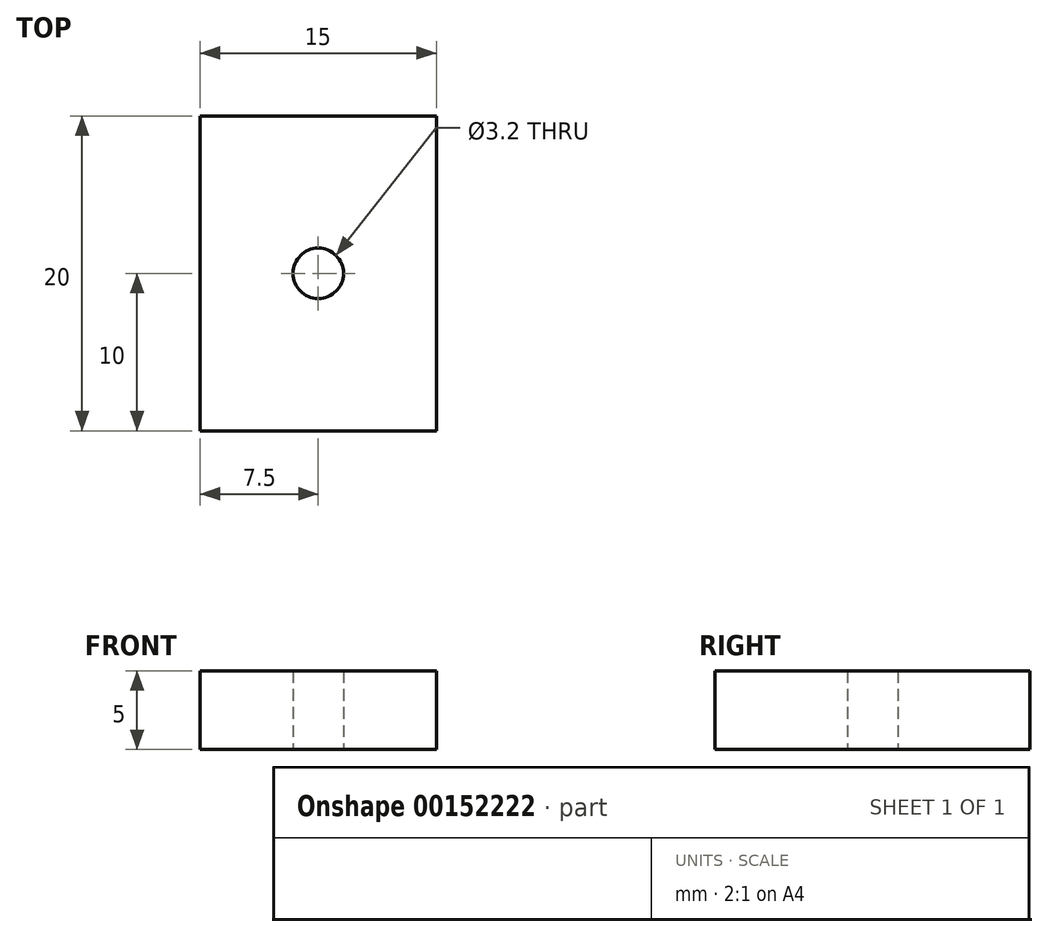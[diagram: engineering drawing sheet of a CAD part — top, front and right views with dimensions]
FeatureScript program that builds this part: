
annotation { "Feature Type Name" : "Feature", "Feature Type Description" : "" }
export const myFeature = defineFeature(function(context is Context, id is Id, definition is map)
    precondition{}
    {
        {
            var Q0;
            Q0=qCreatedBy(makeId("Top.planeOp"),FACE);
            var sketch = newSketch(context, id + "F0", { "sketchPlane" : qUnion([Q0])});
            skLineSegment(sketch, "E0.bottom", {"start": v(0, 0) * mm, "end": v(15, 0) * mm});
            skLineSegment(sketch, "E0.top", {"start": v(0, 20) * mm, "end": v(15, 20) * mm});
            skLineSegment(sketch, "E0.left", {"start": v(0, 0) * mm, "end": v(0, 20) * mm});
            skLineSegment(sketch, "E0.right", {"start": v(15, 0) * mm, "end": v(15, 20) * mm});
            skLineSegment(sketch, "E1", {"start": v(0, 10) * mm, "end": v(15, 10) * mm});
            skCircle(sketch, "E2", {"center": v(7.5, 10) * mm, "radius": 1.6 * mm});
            skSolve(sketch);
        }
        {
            var Q0;
            Q0 = qSketchRegion(id + "F0", true);
            extrude(context, id + "F1", {"entities" : qUnion([Q0]), "depth" : 5 * mm, "offsetDistance" : 25 * mm});
        }
    });
